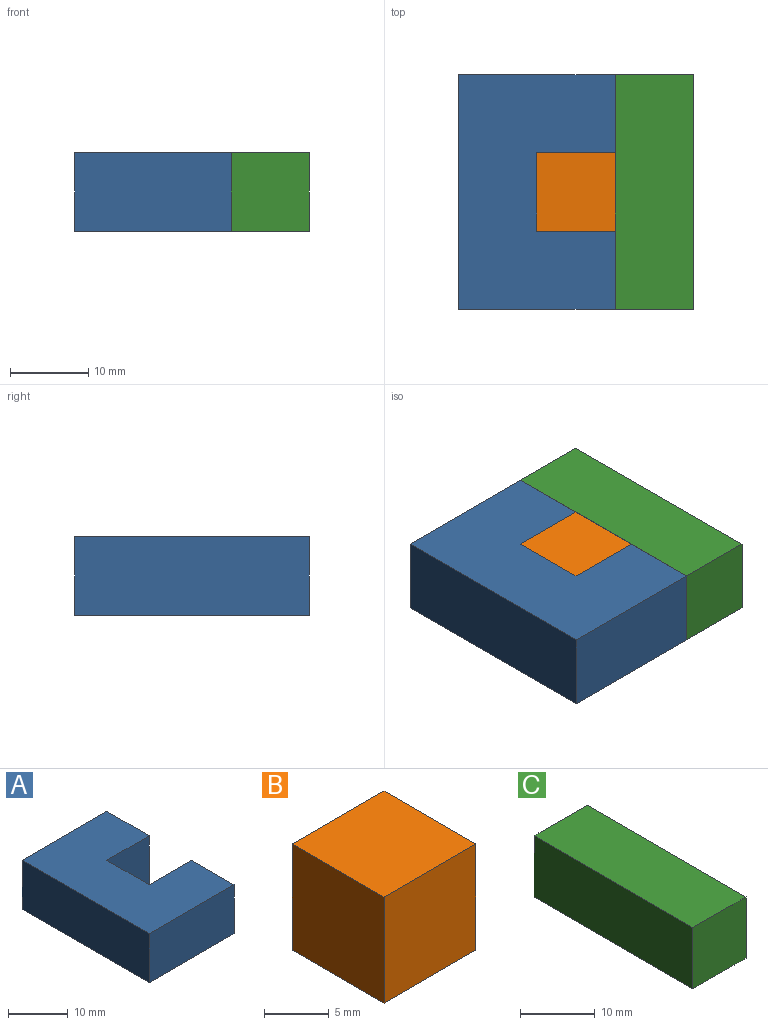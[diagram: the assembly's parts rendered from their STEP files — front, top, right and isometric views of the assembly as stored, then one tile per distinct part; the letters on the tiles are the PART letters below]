
ASSEMBLY  parts=3 mates=2
PART A: 10 faces, bbox 20x30x10 mm
  f0: plane 10x10mm, normal (1,0,0), area 100mm2, adj f1,f7,f8,f9
  f1: plane 20x10mm, normal (0,1,0), area 200mm2, adj f0,f2,f8,f9
  f2: plane 30x10mm, normal (-1,0,0), area 300mm2, adj f1,f3,f8,f9
  f3: plane 20x10mm, normal (0,-1,0), area 200mm2, adj f2,f4,f8,f9
  f4: plane 10x10mm, normal (1,0,0), area 100mm2, adj f3,f5,f8,f9
  f5: plane 10x10mm, normal (0,1,0), area 100mm2, adj f4,f6,f8,f9
  f6: plane 10x10mm, normal (1,0,0), area 100mm2, adj f5,f7,f8,f9
  f7: plane 10x10mm, normal (0,-1,0), area 100mm2, adj f0,f6,f8,f9
  f8: plane 30x20mm, normal (0,0,1), area 500mm2, adj f0,f1,f2,f3,f4,f5,f6,f7
  f9: plane 30x20mm, normal (0,0,-1), area 500mm2, adj f0,f1,f2,f3,f4,f5,f6,f7
PART B: 6 faces, bbox 10x10x10 mm
  f0: plane 10x10mm, normal (1,0,0), area 100mm2, adj f1,f3,f4,f5
  f1: plane 10x10mm, normal (0,1,0), area 100mm2, adj f0,f2,f4,f5
  f2: plane 10x10mm, normal (-1,0,0), area 100mm2, adj f1,f3,f4,f5
  f3: plane 10x10mm, normal (0,-1,0), area 100mm2, adj f0,f2,f4,f5
  f4: plane 10x10mm, normal (0,0,1), area 100mm2, adj f0,f1,f2,f3
  f5: plane 10x10mm, normal (0,0,-1), area 100mm2, adj f0,f1,f2,f3
PART C: 6 faces, bbox 10x30x10 mm
  f0: plane 10x10mm, normal (0,-1,0), area 100mm2, adj f1,f3,f4,f5
  f1: plane 30x10mm, normal (1,0,0), area 300mm2, adj f0,f2,f4,f5
  f2: plane 10x10mm, normal (0,1,0), area 100mm2, adj f1,f3,f4,f5
  f3: plane 30x10mm, normal (-1,0,0), area 300mm2, adj f0,f2,f4,f5
  f4: plane 30x10mm, normal (0,0,1), area 300mm2, adj f0,f1,f2,f3
  f5: plane 30x10mm, normal (0,0,-1), area 300mm2, adj f0,f1,f2,f3
PLACE A t=(31.58,-1.51,-0.1)mm
PLACE B t=(38.89,-6.62,-0.1)mm
PLACE C t=(56.66,-22.62,-0.1)mm
MATE planar A.f6 <-> B.f2  axis (1,0,0) through (-17.44,-3.91,4.9)mm
MATE planar C.f3 <-> B.f0  axis (-1,0,0) through (-7.44,-3.91,4.9)mm
